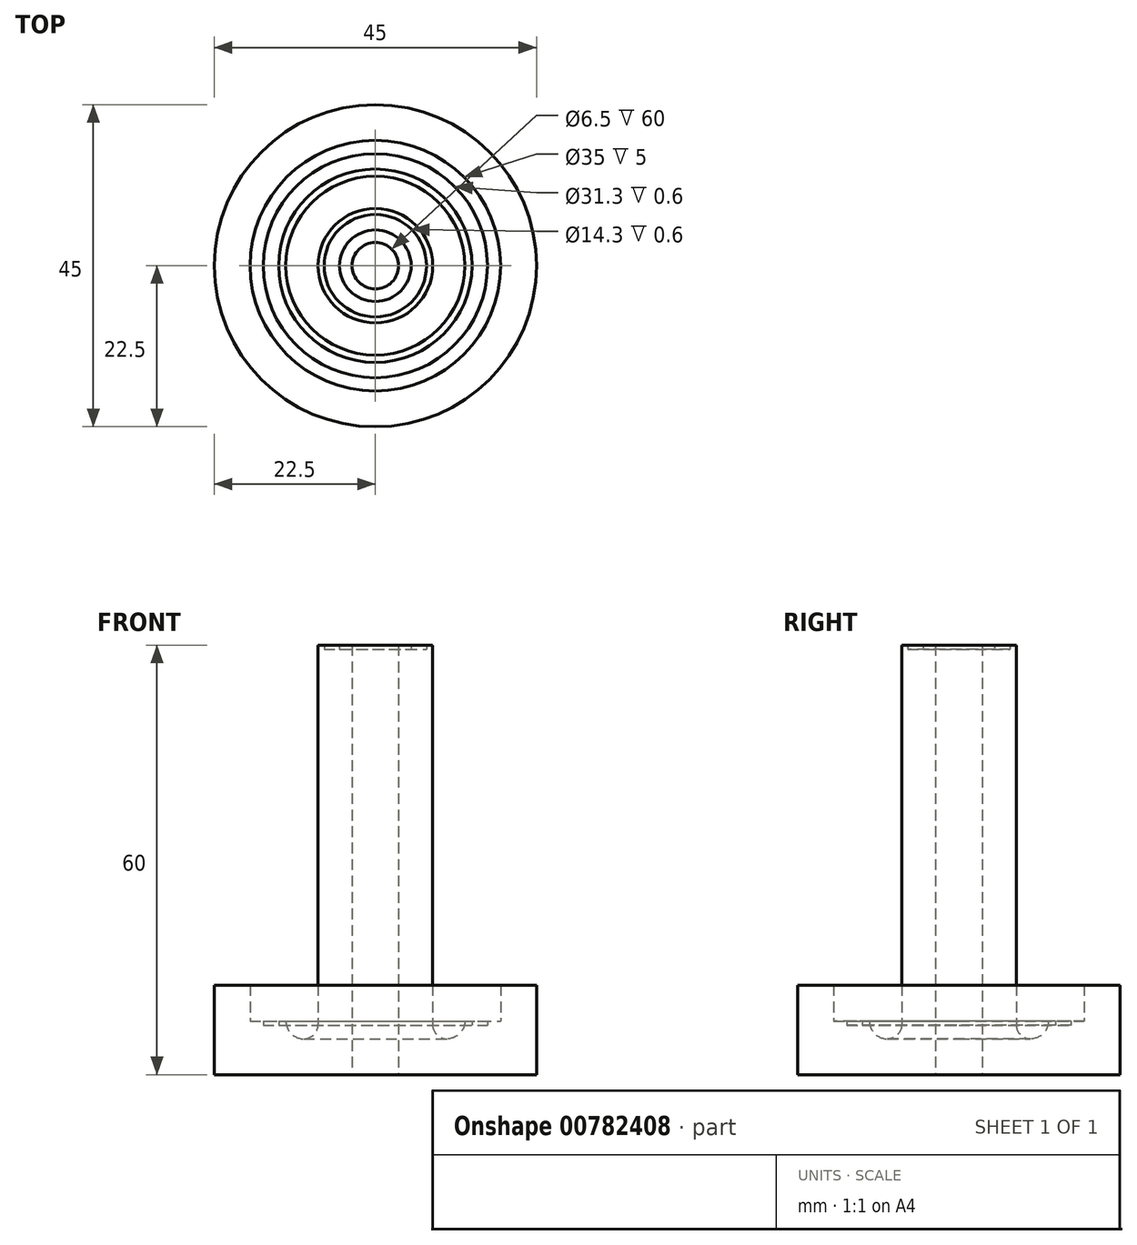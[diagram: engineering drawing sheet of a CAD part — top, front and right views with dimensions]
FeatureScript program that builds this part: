
annotation { "Feature Type Name" : "Feature", "Feature Type Description" : "" }
export const myFeature = defineFeature(function(context is Context, id is Id, definition is map)
    precondition{}
    {
        {
            var Q0;
            Q0=qCreatedBy(makeId("Front.planeOp"),FACE);
            var sketch = newSketch(context, id + "F0", { "sketchPlane" : qUnion([Q0])});
            skLineSegment(sketch, "E0.bottom", {"start": v(0, 0) * mm, "end": v(10, 0) * mm, "construction": true});
            skLineSegment(sketch, "E0.left", {"start": v(0, 0) * mm, "end": v(0, 100) * mm, "construction": true});
            skLineSegment(sketch, "E0.right", {"start": v(10, 0) * mm, "end": v(10, 100) * mm, "construction": true});
            skLineSegment(sketch, "E1.MirrorCS", {"start": v(3.25, -10) * mm, "end": v(3.25, 50) * mm});
            skLineSegment(sketch, "E2.MirrorCS", {"start": v(8, -3) * mm, "end": v(8, 50) * mm});
            skLineSegment(sketch, "E3.MirrorCS", {"start": v(3.25, -10) * mm, "end": v(17.5, -10) * mm});
            skLineSegment(sketch, "E4.MirrorCS", {"start": v(12.5, -2.5) * mm, "end": v(13.5, -2.5) * mm});
            skArc(sketch, "E5.MirrorCS", {"start": v(10, 0) * mm, "mid": v(12.5, -2.5) * mm, "end": v(10, -5) * mm});
            skArc(sketch, "E6.MirrorCS", {"start": v(10, -5) * mm, "mid": v(8.59, -4.41) * mm, "end": v(8, -3) * mm});
            skLineSegment(sketch, "E7.MirrorCS", {"start": v(17.5, -2.5) * mm, "end": v(17.5, 2.5) * mm});
            skLineSegment(sketch, "E8.MirrorCS", {"start": v(17.5, 2.5) * mm, "end": v(22.5, 2.5) * mm});
            skLineSegment(sketch, "E9.MirrorCS", {"start": v(22.5, 2.5) * mm, "end": v(22.5, -10) * mm});
            skLineSegment(sketch, "E10.MirrorCS", {"start": v(22.5, -10) * mm, "end": v(17.5, -10) * mm});
            skLineSegment(sketch, "E11", {"start": v(0, 50) * mm, "end": v(5, 50) * mm});
            skLineSegment(sketch, "E12", {"start": v(5, 50) * mm, "end": v(5, 49.4) * mm});
            skLineSegment(sketch, "E13", {"start": v(5, 49.4) * mm, "end": v(7.15, 49.4) * mm});
            skLineSegment(sketch, "E14", {"start": v(7.15, 49.4) * mm, "end": v(7.15, 50) * mm});
            skLineSegment(sketch, "E15", {"start": v(7.15, 50) * mm, "end": v(8, 50) * mm});
            skLineSegment(sketch, "E16", {"start": v(0, 0) * mm, "end": v(0, -10) * mm, "construction": true});
            skLineSegment(sketch, "E17", {"start": v(13.5, -3.1) * mm, "end": v(13.5, -2.5) * mm});
            skLineSegment(sketch, "E18", {"start": v(13.5, -3.1) * mm, "end": v(15.65, -3.1) * mm});
            skLineSegment(sketch, "E19", {"start": v(15.65, -3.1) * mm, "end": v(15.65, -2.5) * mm});
            skLineSegment(sketch, "E20.trimOffspring", {"start": v(15.65, -2.5) * mm, "end": v(17.5, -2.5) * mm});
            skSolve(sketch);
        }
        {
            var Q0;
            {var subQ3=sQuery(id+"F0.wireOp",EDGE,"E1.MirrorCS");Q0=makeQuery(id+"F0.imprint","IMPRINT",FACE,{"disambiguationData":[TD([[makeQuery(id+"F0.imprint","IMPRINT",EDGE,{"derivedFrom":subQ3}),-1.0]])]});}
            var Q1;
            Q1=sQuery(id+"F0.wireOp",EDGE,"E0.left");
            revolve(context, id + "F1", {"surfaceOperationType" : NewSurfaceOperationType.NEW, "entities" : qUnion([Q0]), "axis" : qUnion([Q1]), "revolveType" : RevolveType.ONE_DIRECTION, "angle" : 360 * degree});
        }
    });
